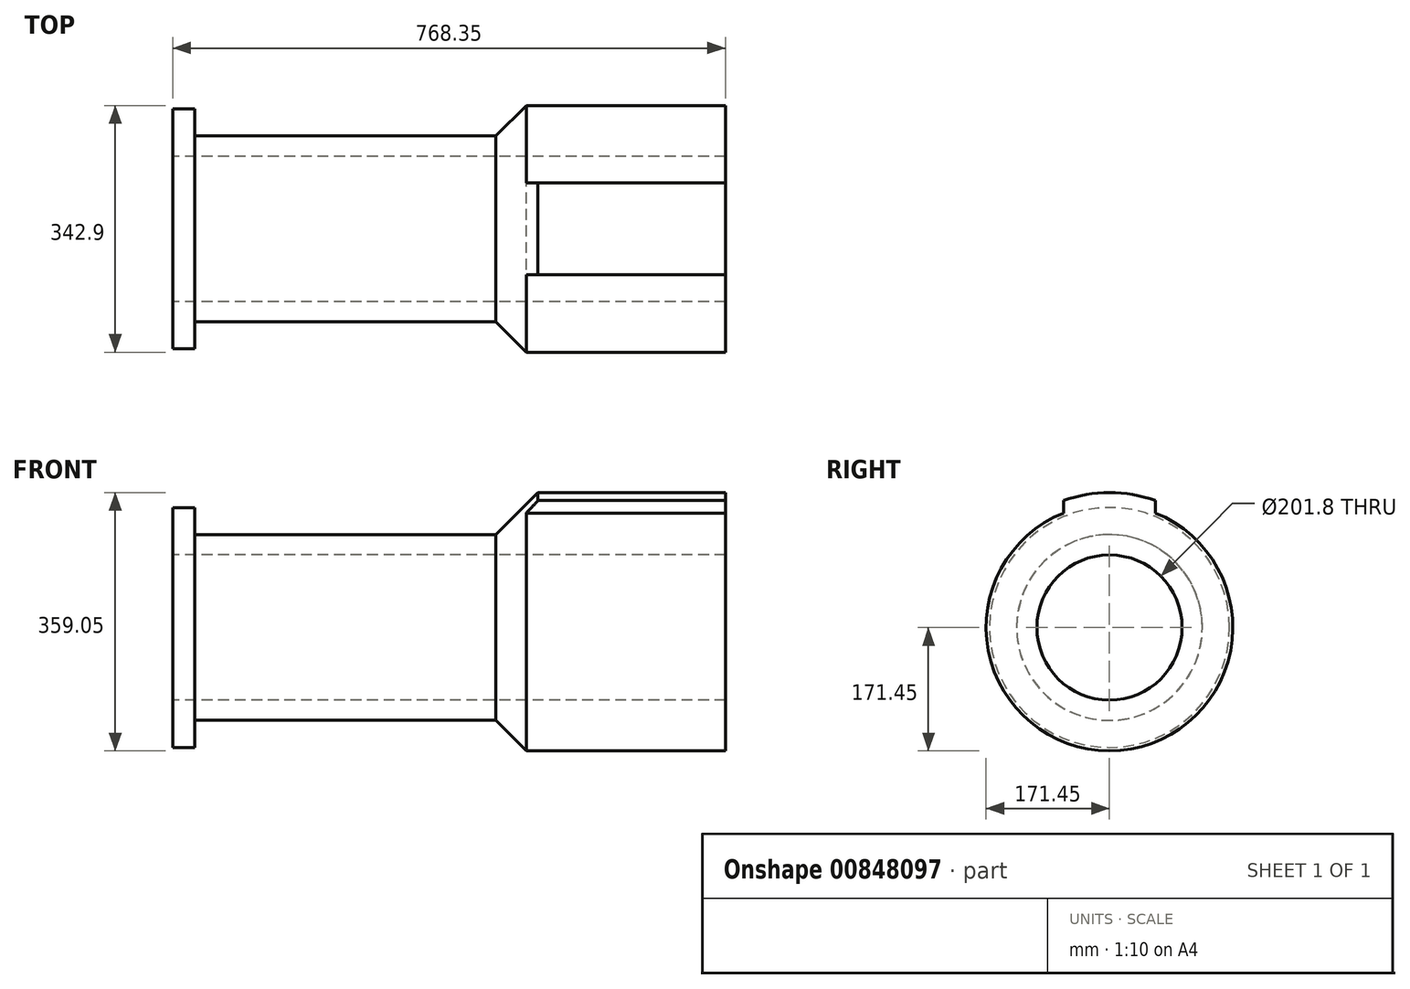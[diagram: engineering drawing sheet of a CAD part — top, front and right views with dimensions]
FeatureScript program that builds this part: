
annotation { "Feature Type Name" : "Feature", "Feature Type Description" : "" }
export const myFeature = defineFeature(function(context is Context, id is Id, definition is map)
    precondition{}
    {
        {
            var Q0;
            Q0=qCreatedBy(makeId("Front.planeOp"),FACE);
            var sketch = newSketch(context, id + "F0", { "sketchPlane" : qUnion([Q0])});
            skLineSegment(sketch, "E0", {"start": v(0, 0) * mm, "end": v(768.35, 0) * mm, "construction": true});
            skLineSegment(sketch, "E1", {"start": v(0, 166.75) * mm, "end": v(30.89, 166.75) * mm});
            skLineSegment(sketch, "E2", {"start": v(30.89, 166.75) * mm, "end": v(30.89, 129.1) * mm});
            skLineSegment(sketch, "E3", {"start": v(30.89, 129.1) * mm, "end": v(449.3, 129.1) * mm});
            skLineSegment(sketch, "E4", {"start": v(768.35, 187.6) * mm, "end": v(768.35, 100.9) * mm});
            skLineSegment(sketch, "E5", {"start": v(768.35, 100.9) * mm, "end": v(0, 100.9) * mm});
            skLineSegment(sketch, "E6", {"start": v(0, 100.9) * mm, "end": v(0, 166.75) * mm});
            skLineSegment(sketch, "E7", {"start": v(449.3, 129.1) * mm, "end": v(507.8, 187.6) * mm});
            skLineSegment(sketch, "E8", {"start": v(507.8, 187.6) * mm, "end": v(768.35, 187.6) * mm});
            skSolve(sketch);
        }
        {
            var Q0;
            Q0 = qSketchRegion(id + "F0", true);
            var Q1;
            Q1=sQuery(id+"F0.wireOp",EDGE,"E0");
            revolve(context, id + "F1", {"surfaceOperationType" : NewSurfaceOperationType.NEW, "entities" : qUnion([Q0]), "axis" : qUnion([Q1]), "revolveType" : RevolveType.FULL});
        }
        {
            var Q0;
            Q0=makeQuery(id+"F1.opRevolve","SWEPT_FACE",FACE,{"disambiguationData":[OSD([sQuery(id+"F0.wireOp",EDGE,"E4")])]});
            var sketch = newSketch(context, id + "F2", { "sketchPlane" : qUnion([Q0])});
            skArc(sketch, "E9", {"start": v(-63.75, 159.16) * mm, "mid": v(0, -171.45) * mm, "end": v(63.75, 159.16) * mm});
            skArc(sketch, "E10", {"start": v(63.75, 178.99) * mm, "mid": v(0, 190) * mm, "end": v(-63.75, 178.99) * mm});
            skLineSegment(sketch, "E11", {"start": v(0, 0) * mm, "end": v(0, 209.24) * mm, "construction": true});
            skLineSegment(sketch, "E12", {"start": v(-63.75, 178.99) * mm, "end": v(-63.75, 159.16) * mm});
            skLineSegment(sketch, "E13", {"start": v(63.75, 178.99) * mm, "end": v(63.75, 159.16) * mm});
            skCircle(sketch, "E14", {"center": v(0, 0) * mm, "radius": 205 * mm});
            skLineSegment(sketch, "E15", {"start": v(0, 0) * mm, "end": v(169.82, -169.82) * mm, "construction": true});
            skLineSegment(sketch, "E16", {"start": v(0, 0) * mm, "end": v(-172.87, -172.87) * mm, "construction": true});
            skSolve(sketch);
        }
        {
            var Q0;
            {var subQ1=sQuery(id+"F2.wireOp",EDGE,"E10");Q0=makeQuery(id+"F2.imprint","IMPRINT",FACE,{"disambiguationData":[TD([[makeQuery(id+"F2.imprint","IMPRINT",EDGE,{"derivedFrom":subQ1}),-1.0]])]});}
            var Q1;
            {var subQ0=sQuery(id+"F2.wireOp",EDGE,"E9");Q1=makeQuery(id+"F2.imprint","IMPRINT",FACE,{"disambiguationData":[TD([[makeQuery(id+"F2.imprint","IMPRINT",EDGE,{"derivedFrom":subQ0}),-1.0]])]});}
            extrude(context, id + "F3", {"entities" : qUnion([Q0, Q1]), "operationType" : NewBodyOperationType.REMOVE, "oppositeDirection" : true, "depth" : 350 * mm, "offsetDistance" : 25 * mm});
        }
    });
